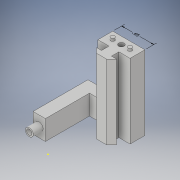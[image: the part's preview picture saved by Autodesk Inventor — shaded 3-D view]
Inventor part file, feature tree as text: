
AUTODESK INVENTOR PART (.ipt)
format: ipt  version: 2018 (Build 220112000, 112)  size: 185,856 bytes
history: native  units: in
note: dims shown in document units (in); Inventor stores cm internally (conversion verified against a paired STEP export)
features: sketch x10, extrude x7, other x2, hole x2
ambient origin geometry x8: Origin, YZ Plane, XZ Plane, XY Plane, X Axis, Y Axis, Z Axis, Center Point
bodies: Solid1 (feature_tree)
feature tree (21):
  other  "Annotations"
  extrude  "Extrusion1"  Depth=0.3in
  extrude  "Extrusion2"  Depth=0.25in
  extrude  "Extrusion3"  Depth=0.05in
  hole  "Hole1"  [1 undecoded]
  extrude  "Extrusion7"  Depth=0.1in
  extrude  "Extrusion8"  Depth=0.15in
  extrude  "Extrusion9"  Depth=0.05in TaperAngle=0.0deg
  sketch  "Sketch16"  dims[d20=0.15in d21=0.08in]
  hole  "Hole3"  [1 undecoded]
  extrude  "Extrusion10"  Depth=0.05in
  sketch  "Sketch1"  dims[d0=0.65in d1=0.3in]
  sketch  "Sketch2"  dims[d2=0.1in d3=0.25in]
  sketch  "Sketch3"  dims[d4=0.2in d5=0.05in]
  sketch  "Sketch6"  dims[d6=0.1in d7=0.1in]
  sketch  "Sketch13"  dims[d8=0.1in d9=0.1in]
  sketch  "Sketch14"  dims[d10=1.5in d11=0.0in d12=0.15in]
  sketch  "Sketch15"  dims[d14=0.08in d18=0.05in d19=0.0in]
  sketch  "Sketch17"  dims[d22=0.05in d23=0.0in d24=0.325in]
  sketch  "Sketch18"  dims[d25=0.11in d26=0.11in d27=0.75in d28=0.375in d29=0.25in d30=0.5635in d31=0.45in d32=0.8108in d68=0.22in d69=0.4in d70=0.5in d71=0.0in d72=0.25in d73=0.4in d77=0.89in d78=0.0in d79=0.125in d80=0.16in d81=0.2in d82=0.0in d83=0.11in d84=0.11in d85=0.75in d86=0.375in d87=0.25in d88=0.5635in d89=0.5in d90=0.8108in d94=0.05in d95=0.0in d91=0.0911in d92=0.1714in d93=0.65in]
  other  "Linear Dimension 1"
note: 2 required parameter values undecoded (feature->parameter linkage not recoverable at this tier; creation-order binding heuristic only, values carry confidence <= 0.55)
